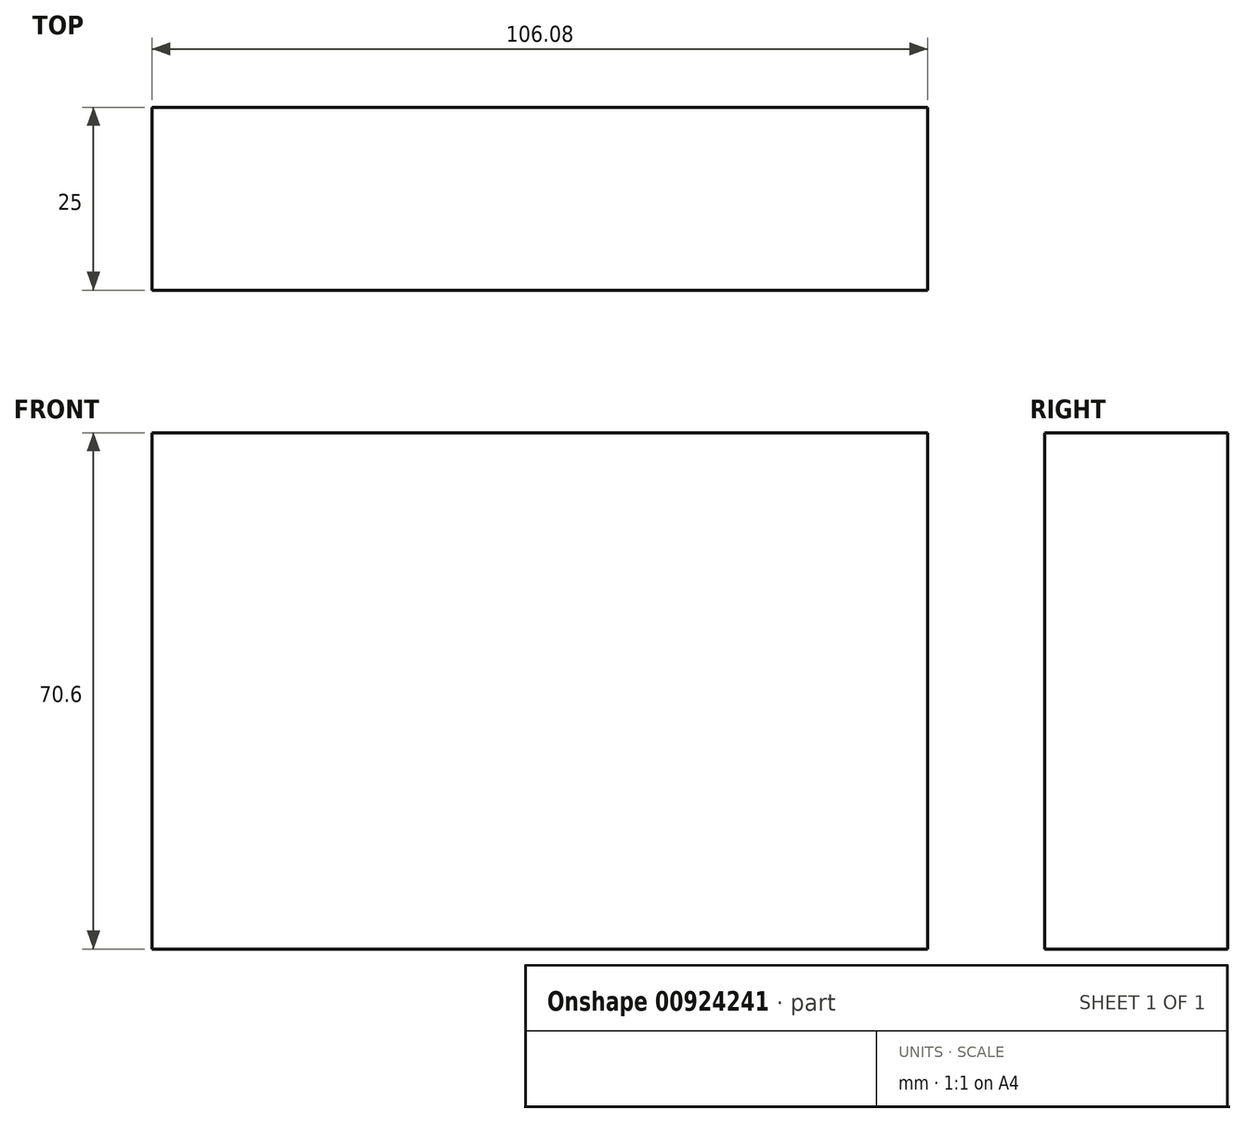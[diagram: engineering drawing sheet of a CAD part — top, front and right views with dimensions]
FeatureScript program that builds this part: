
annotation { "Feature Type Name" : "Feature", "Feature Type Description" : "" }
export const myFeature = defineFeature(function(context is Context, id is Id, definition is map)
    precondition{}
    {
        {
            var Q0;
            Q0=qCreatedBy(makeId("Front.planeOp"),FACE);
            var sketch = newSketch(context, id + "F0", { "sketchPlane" : qUnion([Q0])});
            skLineSegment(sketch, "E0.bottom", {"start": v(-120.76, 39.42) * mm, "end": v(-14.68, 39.42) * mm});
            skLineSegment(sketch, "E0.top", {"start": v(-120.76, -31.18) * mm, "end": v(-14.68, -31.18) * mm});
            skLineSegment(sketch, "E0.left", {"start": v(-120.76, 39.42) * mm, "end": v(-120.76, -31.18) * mm});
            skLineSegment(sketch, "E0.right", {"start": v(-14.68, 39.42) * mm, "end": v(-14.68, -31.18) * mm});
            skSolve(sketch);
        }
        {
            var Q0;
            Q0 = qSketchRegion(id + "F0", true);
            extrude(context, id + "F1", {"entities" : qUnion([Q0]), "depth" : 25 * mm, "offsetDistance" : 25 * mm});
        }
    });
